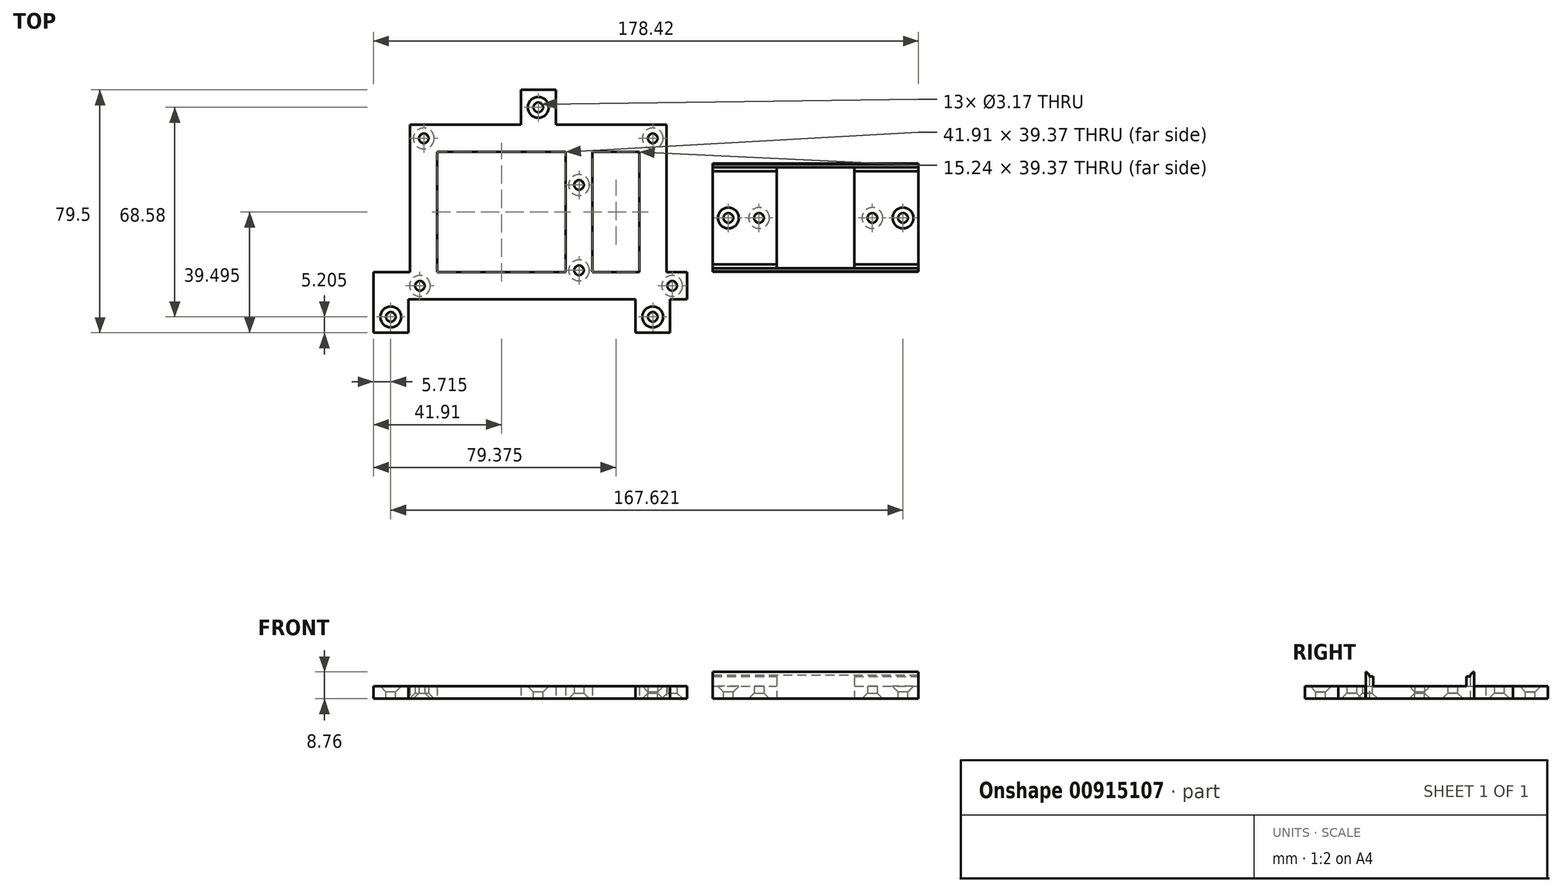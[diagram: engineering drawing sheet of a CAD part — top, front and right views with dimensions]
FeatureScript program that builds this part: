
annotation { "Feature Type Name" : "Feature", "Feature Type Description" : "" }
export const myFeature = defineFeature(function(context is Context, id is Id, definition is map)
    precondition{}
    {
        {
            var Q0;
            Q0=qCreatedBy(makeId("Top.planeOp"),FACE);
            var sketch = newSketch(context, id + "F0", { "sketchPlane" : qUnion([Q0])});
            skLineSegment(sketch, "E0.bottom", {"start": v(30.48, 30.48) * mm, "end": v(-30.48, 30.48) * mm});
            skLineSegment(sketch, "E0.top", {"start": v(30.48, -30.48) * mm, "end": v(-30.48, -30.48) * mm});
            skLineSegment(sketch, "E0.left", {"start": v(30.48, 30.48) * mm, "end": v(30.48, -30.48) * mm});
            skLineSegment(sketch, "E0.right", {"start": v(-30.48, 30.48) * mm, "end": v(-30.48, -30.48) * mm});
            skPoint(sketch, "E0.middle", {"position": v(0, 0) * mm});
            skCircle(sketch, "E1", {"center": v(-25.4, 25.4) * mm, "radius": 2.54 * mm});
            skCircle(sketch, "E2", {"center": v(25.4, 25.4) * mm, "radius": 2.54 * mm});
            skCircle(sketch, "E3", {"center": v(25.4, -25.4) * mm, "radius": 2.54 * mm});
            skCircle(sketch, "E4", {"center": v(-25.4, -25.4) * mm, "radius": 2.54 * mm});
            skLineSegment(sketch, "E5.bottom", {"start": v(21.59, 21.6) * mm, "end": v(-21.59, 21.6) * mm});
            skLineSegment(sketch, "E5.top", {"start": v(21.59, -21.6) * mm, "end": v(-21.59, -21.6) * mm});
            skLineSegment(sketch, "E5.left", {"start": v(21.59, 21.6) * mm, "end": v(21.59, -21.6) * mm});
            skLineSegment(sketch, "E5.right", {"start": v(-21.59, 21.6) * mm, "end": v(-21.59, -21.6) * mm});
            skLineSegment(sketch, "E6.bottom", {"start": v(-30.48, 30.48) * mm, "end": v(-91.44, 30.48) * mm});
            skLineSegment(sketch, "E6.top", {"start": v(-30.48, 21.6) * mm, "end": v(-91.44, 21.6) * mm});
            skLineSegment(sketch, "E6.left", {"start": v(-30.48, 30.48) * mm, "end": v(-30.48, 21.6) * mm});
            skLineSegment(sketch, "E6.right", {"start": v(-91.44, 30.48) * mm, "end": v(-91.44, 21.59) * mm});
            skLineSegment(sketch, "E7.bottom", {"start": v(-30.48, -30.48) * mm, "end": v(-91.44, -30.48) * mm});
            skLineSegment(sketch, "E7.top", {"start": v(-30.48, -21.6) * mm, "end": v(-91.44, -21.6) * mm});
            skLineSegment(sketch, "E7.left", {"start": v(-30.48, -30.48) * mm, "end": v(-30.48, -21.6) * mm});
            skLineSegment(sketch, "E7.right", {"start": v(-91.44, -30.48) * mm, "end": v(-91.44, -21.6) * mm});
            skLineSegment(sketch, "E8.bottom", {"start": v(-91.44, 21.6) * mm, "end": v(-82.55, 21.6) * mm});
            skLineSegment(sketch, "E8.top", {"start": v(-91.44, -21.6) * mm, "end": v(-82.55, -21.6) * mm});
            skLineSegment(sketch, "E8.left", {"start": v(-91.44, 21.59) * mm, "end": v(-91.44, -21.6) * mm});
            skLineSegment(sketch, "E8.right", {"start": v(-82.55, 21.59) * mm, "end": v(-82.55, -21.6) * mm});
            skLineSegment(sketch, "E9.bottom", {"start": v(30.48, 30.48) * mm, "end": v(91.44, 30.48) * mm});
            skLineSegment(sketch, "E9.top", {"start": v(30.48, 21.6) * mm, "end": v(91.44, 21.6) * mm});
            skLineSegment(sketch, "E9.left", {"start": v(30.48, 30.48) * mm, "end": v(30.48, 21.6) * mm});
            skLineSegment(sketch, "E9.right", {"start": v(91.44, 30.48) * mm, "end": v(91.44, 21.6) * mm});
            skLineSegment(sketch, "E10.bottom", {"start": v(30.48, -30.48) * mm, "end": v(91.44, -30.48) * mm});
            skLineSegment(sketch, "E10.top", {"start": v(30.48, -21.6) * mm, "end": v(91.44, -21.6) * mm});
            skLineSegment(sketch, "E10.left", {"start": v(30.48, -30.48) * mm, "end": v(30.48, -21.6) * mm});
            skLineSegment(sketch, "E10.right", {"start": v(91.44, -30.48) * mm, "end": v(91.44, -21.6) * mm});
            skLineSegment(sketch, "E11.bottom", {"start": v(91.44, 21.6) * mm, "end": v(82.55, 21.6) * mm});
            skLineSegment(sketch, "E11.top", {"start": v(91.44, -21.6) * mm, "end": v(82.55, -21.6) * mm});
            skLineSegment(sketch, "E11.left", {"start": v(91.44, 21.6) * mm, "end": v(91.44, -21.6) * mm});
            skLineSegment(sketch, "E11.right", {"start": v(82.55, 21.6) * mm, "end": v(82.55, -21.6) * mm});
            skCircle(sketch, "E12", {"center": v(35.56, 25.4) * mm, "radius": 2.54 * mm});
            skCircle(sketch, "E13", {"center": v(86.36, 25.4) * mm, "radius": 2.54 * mm});
            skCircle(sketch, "E14", {"center": v(86.36, -25.4) * mm, "radius": 2.54 * mm});
            skCircle(sketch, "E15", {"center": v(35.56, -25.4) * mm, "radius": 2.54 * mm});
            skCircle(sketch, "E16", {"center": v(-35.56, 25.4) * mm, "radius": 2.54 * mm});
            skCircle(sketch, "E17", {"center": v(-86.36, 25.4) * mm, "radius": 2.54 * mm});
            skCircle(sketch, "E18", {"center": v(-86.36, -25.4) * mm, "radius": 2.54 * mm});
            skCircle(sketch, "E19", {"center": v(-35.56, -25.4) * mm, "radius": 2.54 * mm});
            skLineSegment(sketch, "E20.bottom", {"start": v(-91.44, 30.48) * mm, "end": v(-80.01, 30.48) * mm});
            skLineSegment(sketch, "E20.top", {"start": v(-91.44, 41.91) * mm, "end": v(-80.01, 41.91) * mm});
            skLineSegment(sketch, "E20.left", {"start": v(-91.44, 30.48) * mm, "end": v(-91.44, 41.91) * mm});
            skLineSegment(sketch, "E20.right", {"start": v(-80.01, 30.48) * mm, "end": v(-80.01, 41.91) * mm});
            skLineSegment(sketch, "E21.bottom", {"start": v(-91.44, -30.48) * mm, "end": v(-80.01, -30.48) * mm});
            skLineSegment(sketch, "E21.top", {"start": v(-91.44, -41.91) * mm, "end": v(-80.01, -41.91) * mm});
            skLineSegment(sketch, "E21.left", {"start": v(-91.44, -30.48) * mm, "end": v(-91.44, -41.91) * mm});
            skLineSegment(sketch, "E21.right", {"start": v(-80.01, -30.48) * mm, "end": v(-80.01, -41.91) * mm});
            skLineSegment(sketch, "E22.bottom", {"start": v(91.44, -30.48) * mm, "end": v(80.01, -30.48) * mm});
            skLineSegment(sketch, "E22.top", {"start": v(91.44, -41.91) * mm, "end": v(80.01, -41.91) * mm});
            skLineSegment(sketch, "E22.left", {"start": v(91.44, -30.48) * mm, "end": v(91.44, -41.91) * mm});
            skLineSegment(sketch, "E22.right", {"start": v(80.01, -30.48) * mm, "end": v(80.01, -41.91) * mm});
            skLineSegment(sketch, "E23.bottom", {"start": v(91.44, 30.48) * mm, "end": v(80.01, 30.48) * mm});
            skLineSegment(sketch, "E23.top", {"start": v(91.44, 41.91) * mm, "end": v(80.01, 41.91) * mm});
            skLineSegment(sketch, "E23.left", {"start": v(91.44, 30.48) * mm, "end": v(91.44, 41.91) * mm});
            skLineSegment(sketch, "E23.right", {"start": v(80.01, 30.48) * mm, "end": v(80.01, 41.91) * mm});
            skLineSegment(sketch, "E24.bottom", {"start": v(-5.72, 30.48) * mm, "end": v(5.71, 30.48) * mm});
            skLineSegment(sketch, "E24.top", {"start": v(-5.72, 41.91) * mm, "end": v(5.71, 41.91) * mm});
            skLineSegment(sketch, "E24.left", {"start": v(-5.72, 30.48) * mm, "end": v(-5.72, 41.91) * mm});
            skLineSegment(sketch, "E24.right", {"start": v(5.71, 30.48) * mm, "end": v(5.71, 41.91) * mm});
            skPoint(sketch, "E25.firstSnap0", {"position": v(-5.72, 36.2) * mm});
            skLineSegment(sketch, "E25.bottom", {"start": v(-5.72, -30.48) * mm, "end": v(5.71, -30.48) * mm});
            skLineSegment(sketch, "E25.top", {"start": v(-5.72, -41.91) * mm, "end": v(5.71, -41.91) * mm});
            skLineSegment(sketch, "E25.left", {"start": v(-5.72, -30.48) * mm, "end": v(-5.72, -41.91) * mm});
            skLineSegment(sketch, "E25.right", {"start": v(5.71, -30.48) * mm, "end": v(5.71, -41.91) * mm});
            skLineSegment(sketch, "E26.bottom", {"start": v(-91.44, 41.91) * mm, "end": v(91.44, 41.91) * mm});
            skLineSegment(sketch, "E26.top", {"start": v(-91.44, 50.8) * mm, "end": v(91.44, 50.8) * mm});
            skLineSegment(sketch, "E26.left", {"start": v(-91.44, 41.91) * mm, "end": v(-91.44, 50.8) * mm});
            skLineSegment(sketch, "E26.right", {"start": v(91.44, 41.91) * mm, "end": v(91.44, 50.8) * mm});
            skPoint(sketch, "E27", {"position": v(-76.2, 46.35) * mm});
            skPoint(sketch, "E27.positionSnap0", {"position": v(-91.44, 46.36) * mm});
            skPoint(sketch, "E28", {"position": v(6.35, 46.36) * mm});
            skPoint(sketch, "E29", {"position": v(0, 94.62) * mm});
            skPoint(sketch, "E30", {"position": v(-74.93, 94.62) * mm});
            skPoint(sketch, "E31", {"position": v(-24.13, 79.38) * mm});
            skPoint(sketch, "E32", {"position": v(-24.13, 51.43) * mm});
            skLineSegment(sketch, "E33.bottom", {"start": v(-79.38, 50.8) * mm, "end": v(-70.49, 50.8) * mm});
            skLineSegment(sketch, "E33.top", {"start": v(-79.38, 99.06) * mm, "end": v(-70.49, 99.06) * mm});
            skLineSegment(sketch, "E33.left", {"start": v(-79.38, 50.8) * mm, "end": v(-79.38, 99.06) * mm});
            skLineSegment(sketch, "E33.right", {"start": v(-70.49, 50.8) * mm, "end": v(-70.49, 99.06) * mm});
            skLineSegment(sketch, "E34.bottom", {"start": v(4.44, 50.8) * mm, "end": v(-4.45, 50.8) * mm});
            skLineSegment(sketch, "E34.top", {"start": v(4.44, 99.06) * mm, "end": v(-4.45, 99.06) * mm});
            skLineSegment(sketch, "E34.left", {"start": v(4.44, 50.8) * mm, "end": v(4.44, 99.06) * mm});
            skLineSegment(sketch, "E34.right", {"start": v(-4.45, 50.8) * mm, "end": v(-4.45, 99.06) * mm});
            skLineSegment(sketch, "E35.bottom", {"start": v(-70.49, 99.06) * mm, "end": v(-4.45, 99.06) * mm});
            skLineSegment(sketch, "E35.top", {"start": v(-70.49, 90.17) * mm, "end": v(-4.45, 90.17) * mm});
            skLineSegment(sketch, "E35.left", {"start": v(-70.49, 99.06) * mm, "end": v(-70.49, 90.17) * mm});
            skLineSegment(sketch, "E35.right", {"start": v(-4.45, 99.06) * mm, "end": v(-4.45, 90.17) * mm});
            skLineSegment(sketch, "E36.bottom", {"start": v(-28.58, 90.17) * mm, "end": v(-19.69, 90.17) * mm});
            skLineSegment(sketch, "E36.top", {"start": v(-28.58, 50.8) * mm, "end": v(-19.69, 50.8) * mm});
            skLineSegment(sketch, "E36.left", {"start": v(-28.58, 90.17) * mm, "end": v(-28.58, 50.8) * mm});
            skLineSegment(sketch, "E36.right", {"start": v(-19.69, 90.17) * mm, "end": v(-19.69, 50.8) * mm});
            skLineSegment(sketch, "E37.bottom", {"start": v(19.67, 50.8) * mm, "end": v(86.98, 50.8) * mm});
            skLineSegment(sketch, "E37.top", {"start": v(19.67, 86.36) * mm, "end": v(86.98, 86.36) * mm});
            skLineSegment(sketch, "E37.left", {"start": v(19.67, 50.8) * mm, "end": v(19.67, 86.36) * mm});
            skLineSegment(sketch, "E37.right", {"start": v(86.98, 50.8) * mm, "end": v(86.98, 86.36) * mm});
            skPoint(sketch, "E38", {"position": v(34.78, 68.58) * mm});
            skPoint(sketch, "E38.positionSnap0", {"position": v(19.67, 68.58) * mm});
            skPoint(sketch, "E39", {"position": v(71.86, 68.58) * mm});
            skLineSegment(sketch, "E40.bottom", {"start": v(40.62, 52.07) * mm, "end": v(66.02, 52.07) * mm});
            skLineSegment(sketch, "E40.top", {"start": v(40.62, 85.1) * mm, "end": v(66.02, 85.1) * mm});
            skLineSegment(sketch, "E40.left", {"start": v(40.62, 52.07) * mm, "end": v(40.62, 85.1) * mm});
            skLineSegment(sketch, "E40.right", {"start": v(66.02, 52.07) * mm, "end": v(66.02, 85.1) * mm});
            skLineSegment(sketch, "E41.bottom", {"start": v(-43.18, 99.06) * mm, "end": v(-31.75, 99.06) * mm});
            skLineSegment(sketch, "E41.top", {"start": v(-43.18, 110.5) * mm, "end": v(-31.75, 110.5) * mm});
            skLineSegment(sketch, "E41.left", {"start": v(-43.18, 99.06) * mm, "end": v(-43.18, 110.5) * mm});
            skLineSegment(sketch, "E41.right", {"start": v(-31.75, 99.06) * mm, "end": v(-31.75, 110.5) * mm});
            skSolve(sketch);
        }
        {
            var Q0;
            Q0=makeQuery(id+"F0.imprint","IMPRINT",FACE,{"disambiguationData":[TD([[makeQuery(id+"F0.imprint","IMPRINT",EDGE,{"derivedFrom":sQuery(id+"F0.wireOp",EDGE,"E1")}),-1.0]])]});
            var Q1;
            {var subQ7=sQuery(id+"F0.wireOp",EDGE,"E6.right");Q1=makeQuery(id+"F0.imprint","IMPRINT",FACE,{"disambiguationData":[TD([[makeQuery(id+"F0.imprint","IMPRINT",EDGE,{"derivedFrom":subQ7}),1.0]])]});}
            var Q2;
            {var subQ0=sQuery(id+"F0.wireOp",EDGE,"E8.left");Q2=makeQuery(id+"F0.imprint","IMPRINT",FACE,{"disambiguationData":[TD([[makeQuery(id+"F0.imprint","IMPRINT",EDGE,{"derivedFrom":subQ0}),1.0]])]});}
            var Q3;
            {var subQ4=sQuery(id+"F0.wireOp",EDGE,"E7.right");Q3=makeQuery(id+"F0.imprint","IMPRINT",FACE,{"disambiguationData":[TD([[makeQuery(id+"F0.imprint","IMPRINT",EDGE,{"derivedFrom":subQ4}),-1.0]])]});}
            var Q4;
            {var subQ4=sQuery(id+"F0.wireOp",EDGE,"E9.right");Q4=makeQuery(id+"F0.imprint","IMPRINT",FACE,{"disambiguationData":[TD([[makeQuery(id+"F0.imprint","IMPRINT",EDGE,{"derivedFrom":subQ4}),-1.0]])]});}
            var Q5;
            {var subQ7=sQuery(id+"F0.wireOp",EDGE,"E10.right");Q5=makeQuery(id+"F0.imprint","IMPRINT",FACE,{"disambiguationData":[TD([[makeQuery(id+"F0.imprint","IMPRINT",EDGE,{"derivedFrom":subQ7}),1.0]])]});}
            var Q6;
            {var subQ0=sQuery(id+"F0.wireOp",EDGE,"E11.left");Q6=makeQuery(id+"F0.imprint","IMPRINT",FACE,{"disambiguationData":[TD([[makeQuery(id+"F0.imprint","IMPRINT",EDGE,{"derivedFrom":subQ0}),-1.0]])]});}
            var Q7;
            Q7=makeQuery(id+"F0.imprint","IMPRINT",FACE,{"disambiguationData":[TD([[makeQuery(id+"F0.imprint","IMPRINT",EDGE,{"derivedFrom":sQuery(id+"F0.wireOp",EDGE,"E20.top")}),-1.0]])]});
            var Q8;
            Q8=makeQuery(id+"F0.imprint","IMPRINT",FACE,{"disambiguationData":[TD([[makeQuery(id+"F0.imprint","IMPRINT",EDGE,{"derivedFrom":sQuery(id+"F0.wireOp",EDGE,"E23.top")}),1.0]])]});
            var Q9;
            Q9=makeQuery(id+"F0.imprint","IMPRINT",FACE,{"disambiguationData":[TD([[makeQuery(id+"F0.imprint","IMPRINT",EDGE,{"derivedFrom":sQuery(id+"F0.wireOp",EDGE,"E22.top")}),-1.0]])]});
            var Q10;
            Q10=makeQuery(id+"F0.imprint","IMPRINT",FACE,{"disambiguationData":[TD([[makeQuery(id+"F0.imprint","IMPRINT",EDGE,{"derivedFrom":sQuery(id+"F0.wireOp",EDGE,"E21.top")}),1.0]])]});
            var Q11;
            Q11=makeQuery(id+"F0.imprint","IMPRINT",FACE,{"disambiguationData":[TD([[makeQuery(id+"F0.imprint","IMPRINT",EDGE,{"derivedFrom":sQuery(id+"F0.wireOp",EDGE,"E24.top")}),-1.0]])]});
            var Q12;
            Q12=makeQuery(id+"F0.imprint","IMPRINT",FACE,{"disambiguationData":[TD([[makeQuery(id+"F0.imprint","IMPRINT",EDGE,{"derivedFrom":sQuery(id+"F0.wireOp",EDGE,"E25.top")}),1.0]])]});
            var Q13;
            {var subQ6=sQuery(id+"F0.wireOp",EDGE,"E20.top");Q13=makeQuery(id+"F0.imprint","IMPRINT",FACE,{"disambiguationData":[TD([[makeQuery(id+"F0.imprint","IMPRINT",EDGE,{"derivedFrom":subQ6}),1.0]])]});}
            var Q14;
            {var subQ4=sQuery(id+"F0.wireOp",EDGE,"E33.top");Q14=makeQuery(id+"F0.imprint","IMPRINT",FACE,{"disambiguationData":[TD([[makeQuery(id+"F0.imprint","IMPRINT",EDGE,{"derivedFrom":subQ4}),-1.0]])]});}
            var Q15;
            {var subQ0=sQuery(id+"F0.wireOp",EDGE,"E35.bottom");var subQ8=makeQuery(id+"F0.imprint","INTERSECT",VERTEX,{"derivedFrom":[subQ0,sQuery(id+"F0.wireOp",EDGE,"E41.right")]});Q15=makeQuery(id+"F0.imprint","IMPRINT",FACE,{"disambiguationData":[TD([[makeQuery(id+"F0.imprint","IMPRINT",EDGE,{"disambiguationData":[TD([[subQ8,1.0]])],"derivedFrom":subQ0}),-1.0]])]});}
            var Q16;
            {var subQ0=sQuery(id+"F0.wireOp",EDGE,"E36.left");Q16=makeQuery(id+"F0.imprint","IMPRINT",FACE,{"disambiguationData":[TD([[makeQuery(id+"F0.imprint","IMPRINT",EDGE,{"derivedFrom":subQ0}),1.0]])]});}
            var Q17;
            {var subQ5=sQuery(id+"F0.wireOp",EDGE,"E34.top");Q17=makeQuery(id+"F0.imprint","IMPRINT",FACE,{"disambiguationData":[TD([[makeQuery(id+"F0.imprint","IMPRINT",EDGE,{"derivedFrom":subQ5}),1.0]])]});}
            var Q18;
            Q18=makeQuery(id+"F0.imprint","IMPRINT",FACE,{"disambiguationData":[TD([[makeQuery(id+"F0.imprint","IMPRINT",EDGE,{"derivedFrom":sQuery(id+"F0.wireOp",EDGE,"E37.top")}),-1.0]])]});
            var Q19;
            Q19=makeQuery(id+"F0.imprint","IMPRINT",FACE,{"disambiguationData":[TD([[makeQuery(id+"F0.imprint","IMPRINT",EDGE,{"derivedFrom":sQuery(id+"F0.wireOp",EDGE,"E41.top")}),-1.0]])]});
            extrude(context, id + "F1", {"entities" : qUnion([Q0, Q1, Q2, Q3, Q4, Q5, Q6, Q7, Q8, Q9, Q10, Q11, Q12, Q13, Q14, Q15, Q16, Q17, Q18, Q19]), "depth" : 4.06 * mm, "offsetDistance" : 25.4 * mm});
        }
        {
            var Q0;
            Q0=makeQuery(id+"F0.imprint","IMPRINT",FACE,{"disambiguationData":[TD([[makeQuery(id+"F0.imprint","IMPRINT",EDGE,{"derivedFrom":sQuery(id+"F0.wireOp",EDGE,"E1")}),1.0]])]});
            var Q1;
            Q1=makeQuery(id+"F0.imprint","IMPRINT",FACE,{"disambiguationData":[TD([[makeQuery(id+"F0.imprint","IMPRINT",EDGE,{"derivedFrom":sQuery(id+"F0.wireOp",EDGE,"E2")}),1.0]])]});
            var Q2;
            Q2=makeQuery(id+"F0.imprint","IMPRINT",FACE,{"disambiguationData":[TD([[makeQuery(id+"F0.imprint","IMPRINT",EDGE,{"derivedFrom":sQuery(id+"F0.wireOp",EDGE,"E3")}),1.0]])]});
            var Q3;
            Q3=makeQuery(id+"F0.imprint","IMPRINT",FACE,{"disambiguationData":[TD([[makeQuery(id+"F0.imprint","IMPRINT",EDGE,{"derivedFrom":sQuery(id+"F0.wireOp",EDGE,"E4")}),1.0]])]});
            var Q4;
            Q4=makeQuery(id+"F0.imprint","IMPRINT",FACE,{"disambiguationData":[TD([[makeQuery(id+"F0.imprint","IMPRINT",EDGE,{"derivedFrom":sQuery(id+"F0.wireOp",EDGE,"E17")}),1.0]])]});
            var Q5;
            Q5=makeQuery(id+"F0.imprint","IMPRINT",FACE,{"disambiguationData":[TD([[makeQuery(id+"F0.imprint","IMPRINT",EDGE,{"derivedFrom":sQuery(id+"F0.wireOp",EDGE,"E18")}),1.0]])]});
            var Q6;
            Q6=makeQuery(id+"F0.imprint","IMPRINT",FACE,{"disambiguationData":[TD([[makeQuery(id+"F0.imprint","IMPRINT",EDGE,{"derivedFrom":sQuery(id+"F0.wireOp",EDGE,"E16")}),1.0]])]});
            var Q7;
            Q7=makeQuery(id+"F0.imprint","IMPRINT",FACE,{"disambiguationData":[TD([[makeQuery(id+"F0.imprint","IMPRINT",EDGE,{"derivedFrom":sQuery(id+"F0.wireOp",EDGE,"E19")}),1.0]])]});
            var Q8;
            Q8=makeQuery(id+"F0.imprint","IMPRINT",FACE,{"disambiguationData":[TD([[makeQuery(id+"F0.imprint","IMPRINT",EDGE,{"derivedFrom":sQuery(id+"F0.wireOp",EDGE,"E15")}),1.0]])]});
            var Q9;
            Q9=makeQuery(id+"F0.imprint","IMPRINT",FACE,{"disambiguationData":[TD([[makeQuery(id+"F0.imprint","IMPRINT",EDGE,{"derivedFrom":sQuery(id+"F0.wireOp",EDGE,"E14")}),1.0]])]});
            var Q10;
            Q10=makeQuery(id+"F0.imprint","IMPRINT",FACE,{"disambiguationData":[TD([[makeQuery(id+"F0.imprint","IMPRINT",EDGE,{"derivedFrom":sQuery(id+"F0.wireOp",EDGE,"E13")}),1.0]])]});
            var Q11;
            Q11=makeQuery(id+"F0.imprint","IMPRINT",FACE,{"disambiguationData":[TD([[makeQuery(id+"F0.imprint","IMPRINT",EDGE,{"derivedFrom":sQuery(id+"F0.wireOp",EDGE,"E12")}),1.0]])]});
            extrude(context, id + "F2", {"entities" : qUnion([Q0, Q1, Q2, Q3, Q4, Q5, Q6, Q7, Q8, Q9, Q10, Q11]), "operationType" : NewBodyOperationType.ADD, "depth" : 7.62 * mm, "offsetDistance" : 25.4 * mm});
        }
        {
            var Q0;
            Q0=sQuery(id+"F0.wireOp",VERTEX,"E1.center");
            var Q1;
            Q1=sQuery(id+"F0.wireOp",VERTEX,"E2.center");
            var Q2;
            Q2=sQuery(id+"F0.wireOp",VERTEX,"E3.center");
            var Q3;
            Q3=sQuery(id+"F0.wireOp",VERTEX,"E4.center");
            var Q4;
            Q4=sQuery(id+"F0.wireOp",VERTEX,"E17.center");
            var Q5;
            Q5=sQuery(id+"F0.wireOp",VERTEX,"E16.center");
            var Q6;
            Q6=sQuery(id+"F0.wireOp",VERTEX,"E18.center");
            var Q7;
            Q7=sQuery(id+"F0.wireOp",VERTEX,"E19.center");
            var Q8;
            Q8=sQuery(id+"F0.wireOp",VERTEX,"E12.center");
            var Q9;
            Q9=sQuery(id+"F0.wireOp",VERTEX,"E13.center");
            var Q10;
            Q10=sQuery(id+"F0.wireOp",VERTEX,"E15.center");
            var Q11;
            Q11=sQuery(id+"F0.wireOp",VERTEX,"E14.center");
            var Q12;
            Q12=makeQuery(id+"F1.opExtrude","SWEPT_BODY",BODY,{"disambiguationData":[OSD([sQuery(id+"F0.wireOp",EDGE,"E0.bottom"),sQuery(id+"F0.wireOp",EDGE,"E0.top"),sQuery(id+"F0.wireOp",EDGE,"E0.left"),sQuery(id+"F0.wireOp",EDGE,"E0.right"),sQuery(id+"F0.wireOp",EDGE,"E1"),sQuery(id+"F0.wireOp",EDGE,"E2"),sQuery(id+"F0.wireOp",EDGE,"E3"),sQuery(id+"F0.wireOp",EDGE,"E4"),sQuery(id+"F0.wireOp",EDGE,"E5.bottom"),sQuery(id+"F0.wireOp",EDGE,"E5.top"),sQuery(id+"F0.wireOp",EDGE,"E5.left"),sQuery(id+"F0.wireOp",EDGE,"E5.right"),sQuery(id+"F0.wireOp",EDGE,"E6.bottom"),sQuery(id+"F0.wireOp",EDGE,"E6.top"),sQuery(id+"F0.wireOp",EDGE,"E6.right"),sQuery(id+"F0.wireOp",EDGE,"E7.bottom"),sQuery(id+"F0.wireOp",EDGE,"E7.top"),sQuery(id+"F0.wireOp",EDGE,"E7.right"),sQuery(id+"F0.wireOp",EDGE,"E8.left"),sQuery(id+"F0.wireOp",EDGE,"E8.right"),sQuery(id+"F0.wireOp",EDGE,"E9.bottom"),sQuery(id+"F0.wireOp",EDGE,"E9.top"),sQuery(id+"F0.wireOp",EDGE,"E9.right"),sQuery(id+"F0.wireOp",EDGE,"E10.bottom"),sQuery(id+"F0.wireOp",EDGE,"E10.top"),sQuery(id+"F0.wireOp",EDGE,"E10.right"),sQuery(id+"F0.wireOp",EDGE,"E11.left"),sQuery(id+"F0.wireOp",EDGE,"E11.right"),sQuery(id+"F0.wireOp",EDGE,"E12"),sQuery(id+"F0.wireOp",EDGE,"E13"),sQuery(id+"F0.wireOp",EDGE,"E14"),sQuery(id+"F0.wireOp",EDGE,"E15"),sQuery(id+"F0.wireOp",EDGE,"E16"),sQuery(id+"F0.wireOp",EDGE,"E17"),sQuery(id+"F0.wireOp",EDGE,"E18"),sQuery(id+"F0.wireOp",EDGE,"E19"),sQuery(id+"F0.wireOp",EDGE,"E20.left"),sQuery(id+"F0.wireOp",EDGE,"E20.right"),sQuery(id+"F0.wireOp",EDGE,"E21.top"),sQuery(id+"F0.wireOp",EDGE,"E21.left"),sQuery(id+"F0.wireOp",EDGE,"E21.right"),sQuery(id+"F0.wireOp",EDGE,"E22.top"),sQuery(id+"F0.wireOp",EDGE,"E22.left"),sQuery(id+"F0.wireOp",EDGE,"E22.right"),sQuery(id+"F0.wireOp",EDGE,"E23.left"),sQuery(id+"F0.wireOp",EDGE,"E23.right"),sQuery(id+"F0.wireOp",EDGE,"E24.left"),sQuery(id+"F0.wireOp",EDGE,"E24.right"),sQuery(id+"F0.wireOp",EDGE,"E25.top"),sQuery(id+"F0.wireOp",EDGE,"E25.left"),sQuery(id+"F0.wireOp",EDGE,"E25.right"),sQuery(id+"F0.wireOp",EDGE,"E26.bottom"),sQuery(id+"F0.wireOp",EDGE,"E26.top"),sQuery(id+"F0.wireOp",EDGE,"E26.left"),sQuery(id+"F0.wireOp",EDGE,"E26.right"),sQuery(id+"F0.wireOp",EDGE,"E33.top"),sQuery(id+"F0.wireOp",EDGE,"E33.left"),sQuery(id+"F0.wireOp",EDGE,"E33.right"),sQuery(id+"F0.wireOp",EDGE,"E34.top"),sQuery(id+"F0.wireOp",EDGE,"E34.left"),sQuery(id+"F0.wireOp",EDGE,"E34.right"),sQuery(id+"F0.wireOp",EDGE,"E35.bottom"),sQuery(id+"F0.wireOp",EDGE,"E35.top"),sQuery(id+"F0.wireOp",EDGE,"E36.left"),sQuery(id+"F0.wireOp",EDGE,"E36.right"),sQuery(id+"F0.wireOp",EDGE,"E37.top"),sQuery(id+"F0.wireOp",EDGE,"E37.left"),sQuery(id+"F0.wireOp",EDGE,"E37.right"),sQuery(id+"F0.wireOp",EDGE,"E40.bottom"),sQuery(id+"F0.wireOp",EDGE,"E40.top"),sQuery(id+"F0.wireOp",EDGE,"E40.left"),sQuery(id+"F0.wireOp",EDGE,"E40.right"),sQuery(id+"F0.wireOp",EDGE,"E41.top"),sQuery(id+"F0.wireOp",EDGE,"E41.left"),sQuery(id+"F0.wireOp",EDGE,"E41.right")])]});
            hole(context, id + "F3", {"style" : HoleStyle.SIMPLE, "endStyle" : HoleEndStyle.THROUGH, "oppositeDirection" : true, "holeDiameter" : 1.27 * mm, "majorDiameter" : 6.35 * mm, "isTappedThrough" : true, "tappedDepth" : 12.7 * mm, "tapClearance" : 3, "locations" : qUnion([Q0, Q1, Q2, Q3, Q4, Q5, Q6, Q7, Q8, Q9, Q10, Q11]), "scope" : qUnion([Q12])});
        }
        {
            var Q0;
            Q0=makeQuery(id+"F1.opExtrude","CAP_FACE",FACE,{"disambiguationData":[OSD([sQuery(id+"F0.wireOp",EDGE,"E0.bottom"),sQuery(id+"F0.wireOp",EDGE,"E0.top"),sQuery(id+"F0.wireOp",EDGE,"E0.left"),sQuery(id+"F0.wireOp",EDGE,"E0.right"),sQuery(id+"F0.wireOp",EDGE,"E1"),sQuery(id+"F0.wireOp",EDGE,"E2"),sQuery(id+"F0.wireOp",EDGE,"E3"),sQuery(id+"F0.wireOp",EDGE,"E4"),sQuery(id+"F0.wireOp",EDGE,"E5.bottom"),sQuery(id+"F0.wireOp",EDGE,"E5.top"),sQuery(id+"F0.wireOp",EDGE,"E5.left"),sQuery(id+"F0.wireOp",EDGE,"E5.right"),sQuery(id+"F0.wireOp",EDGE,"E6.bottom"),sQuery(id+"F0.wireOp",EDGE,"E6.top"),sQuery(id+"F0.wireOp",EDGE,"E6.right"),sQuery(id+"F0.wireOp",EDGE,"E7.bottom"),sQuery(id+"F0.wireOp",EDGE,"E7.top"),sQuery(id+"F0.wireOp",EDGE,"E7.right"),sQuery(id+"F0.wireOp",EDGE,"E8.left"),sQuery(id+"F0.wireOp",EDGE,"E8.right"),sQuery(id+"F0.wireOp",EDGE,"E9.bottom"),sQuery(id+"F0.wireOp",EDGE,"E9.top"),sQuery(id+"F0.wireOp",EDGE,"E9.right"),sQuery(id+"F0.wireOp",EDGE,"E10.bottom"),sQuery(id+"F0.wireOp",EDGE,"E10.top"),sQuery(id+"F0.wireOp",EDGE,"E10.right"),sQuery(id+"F0.wireOp",EDGE,"E11.left"),sQuery(id+"F0.wireOp",EDGE,"E11.right"),sQuery(id+"F0.wireOp",EDGE,"E12"),sQuery(id+"F0.wireOp",EDGE,"E13"),sQuery(id+"F0.wireOp",EDGE,"E14"),sQuery(id+"F0.wireOp",EDGE,"E15"),sQuery(id+"F0.wireOp",EDGE,"E16"),sQuery(id+"F0.wireOp",EDGE,"E17"),sQuery(id+"F0.wireOp",EDGE,"E18"),sQuery(id+"F0.wireOp",EDGE,"E19"),sQuery(id+"F0.wireOp",EDGE,"E20.left"),sQuery(id+"F0.wireOp",EDGE,"E20.right"),sQuery(id+"F0.wireOp",EDGE,"E21.top"),sQuery(id+"F0.wireOp",EDGE,"E21.left"),sQuery(id+"F0.wireOp",EDGE,"E21.right"),sQuery(id+"F0.wireOp",EDGE,"E22.top"),sQuery(id+"F0.wireOp",EDGE,"E22.left"),sQuery(id+"F0.wireOp",EDGE,"E22.right"),sQuery(id+"F0.wireOp",EDGE,"E23.left"),sQuery(id+"F0.wireOp",EDGE,"E23.right"),sQuery(id+"F0.wireOp",EDGE,"E24.left"),sQuery(id+"F0.wireOp",EDGE,"E24.right"),sQuery(id+"F0.wireOp",EDGE,"E25.top"),sQuery(id+"F0.wireOp",EDGE,"E25.left"),sQuery(id+"F0.wireOp",EDGE,"E25.right"),sQuery(id+"F0.wireOp",EDGE,"E26.bottom"),sQuery(id+"F0.wireOp",EDGE,"E26.top"),sQuery(id+"F0.wireOp",EDGE,"E26.left"),sQuery(id+"F0.wireOp",EDGE,"E26.right"),sQuery(id+"F0.wireOp",EDGE,"E33.top"),sQuery(id+"F0.wireOp",EDGE,"E33.left"),sQuery(id+"F0.wireOp",EDGE,"E33.right"),sQuery(id+"F0.wireOp",EDGE,"E34.top"),sQuery(id+"F0.wireOp",EDGE,"E34.left"),sQuery(id+"F0.wireOp",EDGE,"E34.right"),sQuery(id+"F0.wireOp",EDGE,"E35.bottom"),sQuery(id+"F0.wireOp",EDGE,"E35.top"),sQuery(id+"F0.wireOp",EDGE,"E36.left"),sQuery(id+"F0.wireOp",EDGE,"E36.right"),sQuery(id+"F0.wireOp",EDGE,"E37.top"),sQuery(id+"F0.wireOp",EDGE,"E37.left"),sQuery(id+"F0.wireOp",EDGE,"E37.right"),sQuery(id+"F0.wireOp",EDGE,"E40.bottom"),sQuery(id+"F0.wireOp",EDGE,"E40.top"),sQuery(id+"F0.wireOp",EDGE,"E40.left"),sQuery(id+"F0.wireOp",EDGE,"E40.right"),sQuery(id+"F0.wireOp",EDGE,"E41.top"),sQuery(id+"F0.wireOp",EDGE,"E41.left"),sQuery(id+"F0.wireOp",EDGE,"E41.right")])],"isStart":false});
            var sketch = newSketch(context, id + "F4", { "sketchPlane" : qUnion([Q0])});
            skPoint(sketch, "E42", {"position": v(-85.73, 36.2) * mm});
            skPoint(sketch, "E43", {"position": v(85.73, 36.2) * mm});
            skPoint(sketch, "E44", {"position": v(85.73, -36.2) * mm});
            skPoint(sketch, "E44.positionSnap0", {"position": v(85.73, -41.91) * mm});
            skPoint(sketch, "E44.positionSnap1", {"position": v(80.01, -36.2) * mm});
            skPoint(sketch, "E45", {"position": v(-85.73, -36.2) * mm});
            skPoint(sketch, "E45.positionSnap0", {"position": v(-85.73, -41.91) * mm});
            skPoint(sketch, "E45.positionSnap1", {"position": v(-80.01, -36.2) * mm});
            skPoint(sketch, "E46", {"position": v(0, 36.2) * mm});
            skPoint(sketch, "E47", {"position": v(0, -36.2) * mm});
            skPoint(sketch, "E47.positionSnap0", {"position": v(5.71, -36.2) * mm});
            skPoint(sketch, "E48", {"position": v(24.75, 68.58) * mm});
            skPoint(sketch, "E48.positionSnap0", {"position": v(19.67, 68.58) * mm});
            skPoint(sketch, "E49", {"position": v(81.9, 68.58) * mm});
            skPoint(sketch, "E49.positionSnap0", {"position": v(86.98, 68.58) * mm});
            skPoint(sketch, "E50", {"position": v(-37.47, 104.78) * mm});
            skPoint(sketch, "E50.positionSnap0", {"position": v(-37.47, 110.5) * mm});
            skPoint(sketch, "E50.positionSnap1", {"position": v(-43.18, 104.78) * mm});
            skSolve(sketch);
        }
        {
            var Q0;
            Q0=sQuery(id+"F4.wireOp",VERTEX,"E42");
            var Q1;
            Q1=sQuery(id+"F4.wireOp",VERTEX,"E45");
            var Q2;
            Q2=sQuery(id+"F4.wireOp",VERTEX,"E44");
            var Q3;
            Q3=sQuery(id+"F4.wireOp",VERTEX,"E43");
            var Q4;
            Q4=sQuery(id+"F4.wireOp",VERTEX,"E46");
            var Q5;
            Q5=sQuery(id+"F4.wireOp",VERTEX,"E47");
            var Q6;
            Q6=sQuery(id+"F4.wireOp",VERTEX,"E50");
            var Q7;
            Q7=sQuery(id+"F4.wireOp",VERTEX,"E48");
            var Q8;
            Q8=sQuery(id+"F4.wireOp",VERTEX,"E49");
            var Q9;
            Q9=makeQuery(id+"F1.opExtrude","SWEPT_BODY",BODY,{"disambiguationData":[OSD([sQuery(id+"F0.wireOp",EDGE,"E0.bottom"),sQuery(id+"F0.wireOp",EDGE,"E0.top"),sQuery(id+"F0.wireOp",EDGE,"E0.left"),sQuery(id+"F0.wireOp",EDGE,"E0.right"),sQuery(id+"F0.wireOp",EDGE,"E1"),sQuery(id+"F0.wireOp",EDGE,"E2"),sQuery(id+"F0.wireOp",EDGE,"E3"),sQuery(id+"F0.wireOp",EDGE,"E4"),sQuery(id+"F0.wireOp",EDGE,"E5.bottom"),sQuery(id+"F0.wireOp",EDGE,"E5.top"),sQuery(id+"F0.wireOp",EDGE,"E5.left"),sQuery(id+"F0.wireOp",EDGE,"E5.right"),sQuery(id+"F0.wireOp",EDGE,"E6.bottom"),sQuery(id+"F0.wireOp",EDGE,"E6.top"),sQuery(id+"F0.wireOp",EDGE,"E6.right"),sQuery(id+"F0.wireOp",EDGE,"E7.bottom"),sQuery(id+"F0.wireOp",EDGE,"E7.top"),sQuery(id+"F0.wireOp",EDGE,"E7.right"),sQuery(id+"F0.wireOp",EDGE,"E8.left"),sQuery(id+"F0.wireOp",EDGE,"E8.right"),sQuery(id+"F0.wireOp",EDGE,"E9.bottom"),sQuery(id+"F0.wireOp",EDGE,"E9.top"),sQuery(id+"F0.wireOp",EDGE,"E9.right"),sQuery(id+"F0.wireOp",EDGE,"E10.bottom"),sQuery(id+"F0.wireOp",EDGE,"E10.top"),sQuery(id+"F0.wireOp",EDGE,"E10.right"),sQuery(id+"F0.wireOp",EDGE,"E11.left"),sQuery(id+"F0.wireOp",EDGE,"E11.right"),sQuery(id+"F0.wireOp",EDGE,"E12"),sQuery(id+"F0.wireOp",EDGE,"E13"),sQuery(id+"F0.wireOp",EDGE,"E14"),sQuery(id+"F0.wireOp",EDGE,"E15"),sQuery(id+"F0.wireOp",EDGE,"E16"),sQuery(id+"F0.wireOp",EDGE,"E17"),sQuery(id+"F0.wireOp",EDGE,"E18"),sQuery(id+"F0.wireOp",EDGE,"E19"),sQuery(id+"F0.wireOp",EDGE,"E20.left"),sQuery(id+"F0.wireOp",EDGE,"E20.right"),sQuery(id+"F0.wireOp",EDGE,"E21.top"),sQuery(id+"F0.wireOp",EDGE,"E21.left"),sQuery(id+"F0.wireOp",EDGE,"E21.right"),sQuery(id+"F0.wireOp",EDGE,"E22.top"),sQuery(id+"F0.wireOp",EDGE,"E22.left"),sQuery(id+"F0.wireOp",EDGE,"E22.right"),sQuery(id+"F0.wireOp",EDGE,"E23.left"),sQuery(id+"F0.wireOp",EDGE,"E23.right"),sQuery(id+"F0.wireOp",EDGE,"E24.left"),sQuery(id+"F0.wireOp",EDGE,"E24.right"),sQuery(id+"F0.wireOp",EDGE,"E25.top"),sQuery(id+"F0.wireOp",EDGE,"E25.left"),sQuery(id+"F0.wireOp",EDGE,"E25.right"),sQuery(id+"F0.wireOp",EDGE,"E26.bottom"),sQuery(id+"F0.wireOp",EDGE,"E26.top"),sQuery(id+"F0.wireOp",EDGE,"E26.left"),sQuery(id+"F0.wireOp",EDGE,"E26.right"),sQuery(id+"F0.wireOp",EDGE,"E33.top"),sQuery(id+"F0.wireOp",EDGE,"E33.left"),sQuery(id+"F0.wireOp",EDGE,"E33.right"),sQuery(id+"F0.wireOp",EDGE,"E34.top"),sQuery(id+"F0.wireOp",EDGE,"E34.left"),sQuery(id+"F0.wireOp",EDGE,"E34.right"),sQuery(id+"F0.wireOp",EDGE,"E35.bottom"),sQuery(id+"F0.wireOp",EDGE,"E35.top"),sQuery(id+"F0.wireOp",EDGE,"E36.left"),sQuery(id+"F0.wireOp",EDGE,"E36.right"),sQuery(id+"F0.wireOp",EDGE,"E37.top"),sQuery(id+"F0.wireOp",EDGE,"E37.left"),sQuery(id+"F0.wireOp",EDGE,"E37.right"),sQuery(id+"F0.wireOp",EDGE,"E40.bottom"),sQuery(id+"F0.wireOp",EDGE,"E40.top"),sQuery(id+"F0.wireOp",EDGE,"E40.left"),sQuery(id+"F0.wireOp",EDGE,"E40.right"),sQuery(id+"F0.wireOp",EDGE,"E41.top"),sQuery(id+"F0.wireOp",EDGE,"E41.left"),sQuery(id+"F0.wireOp",EDGE,"E41.right")])]});
            hole(context, id + "F5", {"style" : HoleStyle.C_SINK, "endStyle" : HoleEndStyle.THROUGH, "holeDiameter" : 3.17 * mm, "cSinkDiameter" : 6.86 * mm, "cSinkAngle" : 90 * degree, "majorDiameter" : 6.35 * mm, "isTappedThrough" : true, "tappedDepth" : 12.7 * mm, "tapClearance" : 3, "locations" : qUnion([Q0, Q1, Q2, Q3, Q4, Q5, Q6, Q7, Q8]), "scope" : qUnion([Q9])});
        }
        {
            var Q0;
            Q0=sQuery(id+"F0.wireOp",VERTEX,"E27");
            var Q1;
            Q1=sQuery(id+"F0.wireOp",VERTEX,"E30");
            var Q2;
            Q2=sQuery(id+"F0.wireOp",VERTEX,"E31");
            var Q3;
            Q3=sQuery(id+"F0.wireOp",VERTEX,"E32");
            var Q4;
            Q4=sQuery(id+"F0.wireOp",VERTEX,"E28");
            var Q5;
            Q5=sQuery(id+"F0.wireOp",VERTEX,"E29");
            var Q6;
            Q6=sQuery(id+"F0.wireOp",VERTEX,"E38");
            var Q7;
            Q7=sQuery(id+"F0.wireOp",VERTEX,"E39");
            var Q8;
            Q8=makeQuery(id+"F1.opExtrude","SWEPT_BODY",BODY,{"disambiguationData":[OSD([sQuery(id+"F0.wireOp",EDGE,"E0.bottom"),sQuery(id+"F0.wireOp",EDGE,"E0.top"),sQuery(id+"F0.wireOp",EDGE,"E0.left"),sQuery(id+"F0.wireOp",EDGE,"E0.right"),sQuery(id+"F0.wireOp",EDGE,"E1"),sQuery(id+"F0.wireOp",EDGE,"E2"),sQuery(id+"F0.wireOp",EDGE,"E3"),sQuery(id+"F0.wireOp",EDGE,"E4"),sQuery(id+"F0.wireOp",EDGE,"E5.bottom"),sQuery(id+"F0.wireOp",EDGE,"E5.top"),sQuery(id+"F0.wireOp",EDGE,"E5.left"),sQuery(id+"F0.wireOp",EDGE,"E5.right"),sQuery(id+"F0.wireOp",EDGE,"E6.bottom"),sQuery(id+"F0.wireOp",EDGE,"E6.top"),sQuery(id+"F0.wireOp",EDGE,"E6.right"),sQuery(id+"F0.wireOp",EDGE,"E7.bottom"),sQuery(id+"F0.wireOp",EDGE,"E7.top"),sQuery(id+"F0.wireOp",EDGE,"E7.right"),sQuery(id+"F0.wireOp",EDGE,"E8.left"),sQuery(id+"F0.wireOp",EDGE,"E8.right"),sQuery(id+"F0.wireOp",EDGE,"E9.bottom"),sQuery(id+"F0.wireOp",EDGE,"E9.top"),sQuery(id+"F0.wireOp",EDGE,"E9.right"),sQuery(id+"F0.wireOp",EDGE,"E10.bottom"),sQuery(id+"F0.wireOp",EDGE,"E10.top"),sQuery(id+"F0.wireOp",EDGE,"E10.right"),sQuery(id+"F0.wireOp",EDGE,"E11.left"),sQuery(id+"F0.wireOp",EDGE,"E11.right"),sQuery(id+"F0.wireOp",EDGE,"E12"),sQuery(id+"F0.wireOp",EDGE,"E13"),sQuery(id+"F0.wireOp",EDGE,"E14"),sQuery(id+"F0.wireOp",EDGE,"E15"),sQuery(id+"F0.wireOp",EDGE,"E16"),sQuery(id+"F0.wireOp",EDGE,"E17"),sQuery(id+"F0.wireOp",EDGE,"E18"),sQuery(id+"F0.wireOp",EDGE,"E19"),sQuery(id+"F0.wireOp",EDGE,"E20.left"),sQuery(id+"F0.wireOp",EDGE,"E20.right"),sQuery(id+"F0.wireOp",EDGE,"E21.top"),sQuery(id+"F0.wireOp",EDGE,"E21.left"),sQuery(id+"F0.wireOp",EDGE,"E21.right"),sQuery(id+"F0.wireOp",EDGE,"E22.top"),sQuery(id+"F0.wireOp",EDGE,"E22.left"),sQuery(id+"F0.wireOp",EDGE,"E22.right"),sQuery(id+"F0.wireOp",EDGE,"E23.left"),sQuery(id+"F0.wireOp",EDGE,"E23.right"),sQuery(id+"F0.wireOp",EDGE,"E24.left"),sQuery(id+"F0.wireOp",EDGE,"E24.right"),sQuery(id+"F0.wireOp",EDGE,"E25.top"),sQuery(id+"F0.wireOp",EDGE,"E25.left"),sQuery(id+"F0.wireOp",EDGE,"E25.right"),sQuery(id+"F0.wireOp",EDGE,"E26.bottom"),sQuery(id+"F0.wireOp",EDGE,"E26.top"),sQuery(id+"F0.wireOp",EDGE,"E26.left"),sQuery(id+"F0.wireOp",EDGE,"E26.right"),sQuery(id+"F0.wireOp",EDGE,"E33.top"),sQuery(id+"F0.wireOp",EDGE,"E33.left"),sQuery(id+"F0.wireOp",EDGE,"E33.right"),sQuery(id+"F0.wireOp",EDGE,"E34.top"),sQuery(id+"F0.wireOp",EDGE,"E34.left"),sQuery(id+"F0.wireOp",EDGE,"E34.right"),sQuery(id+"F0.wireOp",EDGE,"E35.bottom"),sQuery(id+"F0.wireOp",EDGE,"E35.top"),sQuery(id+"F0.wireOp",EDGE,"E36.left"),sQuery(id+"F0.wireOp",EDGE,"E36.right"),sQuery(id+"F0.wireOp",EDGE,"E37.top"),sQuery(id+"F0.wireOp",EDGE,"E37.left"),sQuery(id+"F0.wireOp",EDGE,"E37.right"),sQuery(id+"F0.wireOp",EDGE,"E40.bottom"),sQuery(id+"F0.wireOp",EDGE,"E40.top"),sQuery(id+"F0.wireOp",EDGE,"E40.left"),sQuery(id+"F0.wireOp",EDGE,"E40.right"),sQuery(id+"F0.wireOp",EDGE,"E41.top"),sQuery(id+"F0.wireOp",EDGE,"E41.left"),sQuery(id+"F0.wireOp",EDGE,"E41.right")])]});
            hole(context, id + "F6", {"style" : HoleStyle.C_SINK, "endStyle" : HoleEndStyle.THROUGH, "oppositeDirection" : true, "holeDiameter" : 3.17 * mm, "cSinkDiameter" : 6.86 * mm, "cSinkAngle" : 90 * degree, "majorDiameter" : 6.35 * mm, "isTappedThrough" : true, "tappedDepth" : 12.7 * mm, "tapClearance" : 3, "locations" : qUnion([Q0, Q1, Q2, Q3, Q4, Q5, Q6, Q7]), "scope" : qUnion([Q8])});
        }
        {
            var Q0;
            Q0=makeQuery(id+"F1.opExtrude","CAP_FACE",FACE,{"disambiguationData":[OSD([sQuery(id+"F0.wireOp",EDGE,"E0.bottom"),sQuery(id+"F0.wireOp",EDGE,"E0.top"),sQuery(id+"F0.wireOp",EDGE,"E0.left"),sQuery(id+"F0.wireOp",EDGE,"E0.right"),sQuery(id+"F0.wireOp",EDGE,"E1"),sQuery(id+"F0.wireOp",EDGE,"E2"),sQuery(id+"F0.wireOp",EDGE,"E3"),sQuery(id+"F0.wireOp",EDGE,"E4"),sQuery(id+"F0.wireOp",EDGE,"E5.bottom"),sQuery(id+"F0.wireOp",EDGE,"E5.top"),sQuery(id+"F0.wireOp",EDGE,"E5.left"),sQuery(id+"F0.wireOp",EDGE,"E5.right"),sQuery(id+"F0.wireOp",EDGE,"E6.bottom"),sQuery(id+"F0.wireOp",EDGE,"E6.top"),sQuery(id+"F0.wireOp",EDGE,"E6.right"),sQuery(id+"F0.wireOp",EDGE,"E7.bottom"),sQuery(id+"F0.wireOp",EDGE,"E7.top"),sQuery(id+"F0.wireOp",EDGE,"E7.right"),sQuery(id+"F0.wireOp",EDGE,"E8.left"),sQuery(id+"F0.wireOp",EDGE,"E8.right"),sQuery(id+"F0.wireOp",EDGE,"E9.bottom"),sQuery(id+"F0.wireOp",EDGE,"E9.top"),sQuery(id+"F0.wireOp",EDGE,"E9.right"),sQuery(id+"F0.wireOp",EDGE,"E10.bottom"),sQuery(id+"F0.wireOp",EDGE,"E10.top"),sQuery(id+"F0.wireOp",EDGE,"E10.right"),sQuery(id+"F0.wireOp",EDGE,"E11.left"),sQuery(id+"F0.wireOp",EDGE,"E11.right"),sQuery(id+"F0.wireOp",EDGE,"E12"),sQuery(id+"F0.wireOp",EDGE,"E13"),sQuery(id+"F0.wireOp",EDGE,"E14"),sQuery(id+"F0.wireOp",EDGE,"E15"),sQuery(id+"F0.wireOp",EDGE,"E16"),sQuery(id+"F0.wireOp",EDGE,"E17"),sQuery(id+"F0.wireOp",EDGE,"E18"),sQuery(id+"F0.wireOp",EDGE,"E19"),sQuery(id+"F0.wireOp",EDGE,"E20.left"),sQuery(id+"F0.wireOp",EDGE,"E20.right"),sQuery(id+"F0.wireOp",EDGE,"E21.top"),sQuery(id+"F0.wireOp",EDGE,"E21.left"),sQuery(id+"F0.wireOp",EDGE,"E21.right"),sQuery(id+"F0.wireOp",EDGE,"E22.top"),sQuery(id+"F0.wireOp",EDGE,"E22.left"),sQuery(id+"F0.wireOp",EDGE,"E22.right"),sQuery(id+"F0.wireOp",EDGE,"E23.left"),sQuery(id+"F0.wireOp",EDGE,"E23.right"),sQuery(id+"F0.wireOp",EDGE,"E24.left"),sQuery(id+"F0.wireOp",EDGE,"E24.right"),sQuery(id+"F0.wireOp",EDGE,"E25.top"),sQuery(id+"F0.wireOp",EDGE,"E25.left"),sQuery(id+"F0.wireOp",EDGE,"E25.right"),sQuery(id+"F0.wireOp",EDGE,"E26.bottom"),sQuery(id+"F0.wireOp",EDGE,"E26.top"),sQuery(id+"F0.wireOp",EDGE,"E26.left"),sQuery(id+"F0.wireOp",EDGE,"E26.right"),sQuery(id+"F0.wireOp",EDGE,"E33.top"),sQuery(id+"F0.wireOp",EDGE,"E33.left"),sQuery(id+"F0.wireOp",EDGE,"E33.right"),sQuery(id+"F0.wireOp",EDGE,"E34.top"),sQuery(id+"F0.wireOp",EDGE,"E34.left"),sQuery(id+"F0.wireOp",EDGE,"E34.right"),sQuery(id+"F0.wireOp",EDGE,"E35.bottom"),sQuery(id+"F0.wireOp",EDGE,"E35.top"),sQuery(id+"F0.wireOp",EDGE,"E36.left"),sQuery(id+"F0.wireOp",EDGE,"E36.right"),sQuery(id+"F0.wireOp",EDGE,"E37.top"),sQuery(id+"F0.wireOp",EDGE,"E37.left"),sQuery(id+"F0.wireOp",EDGE,"E37.right"),sQuery(id+"F0.wireOp",EDGE,"E40.bottom"),sQuery(id+"F0.wireOp",EDGE,"E40.top"),sQuery(id+"F0.wireOp",EDGE,"E40.left"),sQuery(id+"F0.wireOp",EDGE,"E40.right"),sQuery(id+"F0.wireOp",EDGE,"E41.top"),sQuery(id+"F0.wireOp",EDGE,"E41.left"),sQuery(id+"F0.wireOp",EDGE,"E41.right")])],"isStart":false});
            var sketch = newSketch(context, id + "F7", { "sketchPlane" : qUnion([Q0])});
            skLineSegment(sketch, "E51.bottom", {"start": v(19.67, 86.36) * mm, "end": v(86.98, 86.36) * mm});
            skLineSegment(sketch, "E51.top", {"start": v(19.67, 85.1) * mm, "end": v(86.98, 85.1) * mm});
            skLineSegment(sketch, "E51.left", {"start": v(19.67, 86.36) * mm, "end": v(19.67, 85.1) * mm});
            skLineSegment(sketch, "E51.right", {"start": v(86.98, 86.36) * mm, "end": v(86.98, 85.1) * mm});
            skLineSegment(sketch, "E52.bottom", {"start": v(19.67, 50.8) * mm, "end": v(86.98, 50.8) * mm});
            skLineSegment(sketch, "E52.top", {"start": v(19.67, 52.07) * mm, "end": v(86.98, 52.07) * mm});
            skLineSegment(sketch, "E52.left", {"start": v(19.67, 50.8) * mm, "end": v(19.67, 52.07) * mm});
            skLineSegment(sketch, "E52.right", {"start": v(86.98, 50.8) * mm, "end": v(86.98, 52.07) * mm});
            skLineSegment(sketch, "E53.top", {"start": v(19.67, 53.34) * mm, "end": v(86.98, 53.34) * mm});
            skLineSegment(sketch, "E53.left", {"start": v(19.67, 52.07) * mm, "end": v(19.67, 53.34) * mm});
            skLineSegment(sketch, "E53.right", {"start": v(86.98, 52.07) * mm, "end": v(86.98, 53.34) * mm});
            skLineSegment(sketch, "E54.top", {"start": v(19.67, 83.82) * mm, "end": v(86.98, 83.82) * mm});
            skLineSegment(sketch, "E54.left", {"start": v(19.67, 85.1) * mm, "end": v(19.67, 83.82) * mm});
            skLineSegment(sketch, "E54.right", {"start": v(86.98, 85.1) * mm, "end": v(86.98, 83.82) * mm});
            skSolve(sketch);
        }
        {
            var Q0;
            {var subQ3=sQuery(id+"F7.wireOp",EDGE,"E54.left");Q0=makeQuery(id+"F7.imprint","IMPRINT",FACE,{"disambiguationData":[TD([[makeQuery(id+"F7.imprint","IMPRINT",EDGE,{"derivedFrom":subQ3}),-1.0]])]});}
            var Q1;
            {var subQ3=sQuery(id+"F7.wireOp",EDGE,"E54.right");Q1=makeQuery(id+"F7.imprint","IMPRINT",FACE,{"disambiguationData":[TD([[makeQuery(id+"F7.imprint","IMPRINT",EDGE,{"derivedFrom":subQ3}),1.0]])]});}
            var Q2;
            {var subQ3=sQuery(id+"F7.wireOp",EDGE,"E53.left");Q2=makeQuery(id+"F7.imprint","IMPRINT",FACE,{"disambiguationData":[TD([[makeQuery(id+"F7.imprint","IMPRINT",EDGE,{"derivedFrom":subQ3}),-1.0]])]});}
            var Q3;
            {var subQ3=sQuery(id+"F7.wireOp",EDGE,"E53.right");Q3=makeQuery(id+"F7.imprint","IMPRINT",FACE,{"disambiguationData":[TD([[makeQuery(id+"F7.imprint","IMPRINT",EDGE,{"derivedFrom":subQ3}),1.0]])]});}
            extrude(context, id + "F8", {"entities" : qUnion([Q0, Q1, Q2, Q3]), "operationType" : NewBodyOperationType.ADD, "depth" : 3.17 * mm, "offsetDistance" : 25.4 * mm});
        }
        {
            var Q0;
            Q0=makeQuery(id+"F7.imprint","IMPRINT",FACE,{"disambiguationData":[TD([[makeQuery(id+"F7.imprint","IMPRINT",EDGE,{"derivedFrom":sQuery(id+"F7.wireOp",EDGE,"E52.bottom")}),1.0]])]});
            var Q1;
            Q1=makeQuery(id+"F7.imprint","IMPRINT",FACE,{"disambiguationData":[TD([[makeQuery(id+"F7.imprint","IMPRINT",EDGE,{"derivedFrom":sQuery(id+"F7.wireOp",EDGE,"E51.bottom")}),-1.0]])]});
            extrude(context, id + "F9", {"entities" : qUnion([Q0, Q1]), "operationType" : NewBodyOperationType.ADD, "depth" : 4.7 * mm, "offsetDistance" : 25.4 * mm});
        }
        {
            var Q0;
            Q0=makeQuery(id+"F9.opExtrude","CAP_EDGE",EDGE,{"disambiguationData":[OSD([sQuery(id+"F7.wireOp",EDGE,"E52.top")])],"isStart":false});
            var Q1;
            Q1=makeQuery(id+"F9.opExtrude","CAP_EDGE",EDGE,{"disambiguationData":[OSD([sQuery(id+"F7.wireOp",EDGE,"E51.top")])],"isStart":false});
            chamfer(context, id + "F10", {"entities" : qUnion([Q0, Q1]), "width" : 1.02 * mm, "tangentPropagation" : true});
        }
        {
            var Q0;
            Q0=qCreatedBy(makeId("Top.planeOp"),FACE);
            var sketch = newSketch(context, id + "F11", { "sketchPlane" : qUnion([Q0])});
            skLineSegment(sketch, "E55.bottom", {"start": v(-94.02, 31) * mm, "end": v(96.54, 31) * mm});
            skLineSegment(sketch, "E55.top", {"start": v(-94.02, -49.01) * mm, "end": v(96.54, -49.01) * mm});
            skLineSegment(sketch, "E55.left", {"start": v(-94.02, 31) * mm, "end": v(-94.02, -49.01) * mm});
            skLineSegment(sketch, "E55.right", {"start": v(96.54, 31) * mm, "end": v(96.54, -49.01) * mm});
            skSolve(sketch);
        }
        {
            var Q0;
            Q0 = qSketchRegion(id + "F11", true);
            extrude(context, id + "F12", {"entities" : qUnion([Q0]), "operationType" : NewBodyOperationType.REMOVE, "depth" : 7.87 * mm, "offsetDistance" : 25.4 * mm});
        }
        {
            var Q0;
            Q0=qCreatedBy(makeId("Top.planeOp"),FACE);
            var sketch = newSketch(context, id + "F13", { "sketchPlane" : qUnion([Q0])});
            skLineSegment(sketch, "E56.bottom", {"start": v(11.27, 50.96) * mm, "end": v(98.9, 50.96) * mm});
            skLineSegment(sketch, "E56.top", {"start": v(11.27, 22.93) * mm, "end": v(98.9, 22.93) * mm});
            skLineSegment(sketch, "E56.left", {"start": v(11.27, 50.96) * mm, "end": v(11.27, 22.93) * mm});
            skLineSegment(sketch, "E56.right", {"start": v(98.9, 50.96) * mm, "end": v(98.9, 22.93) * mm});
            skSolve(sketch);
        }
        {
            var Q0;
            Q0 = qSketchRegion(id + "F13", true);
            extrude(context, id + "F14", {"entities" : qUnion([Q0]), "operationType" : NewBodyOperationType.REMOVE, "depth" : 10.92 * mm, "offsetDistance" : 25.4 * mm});
        }
    });
